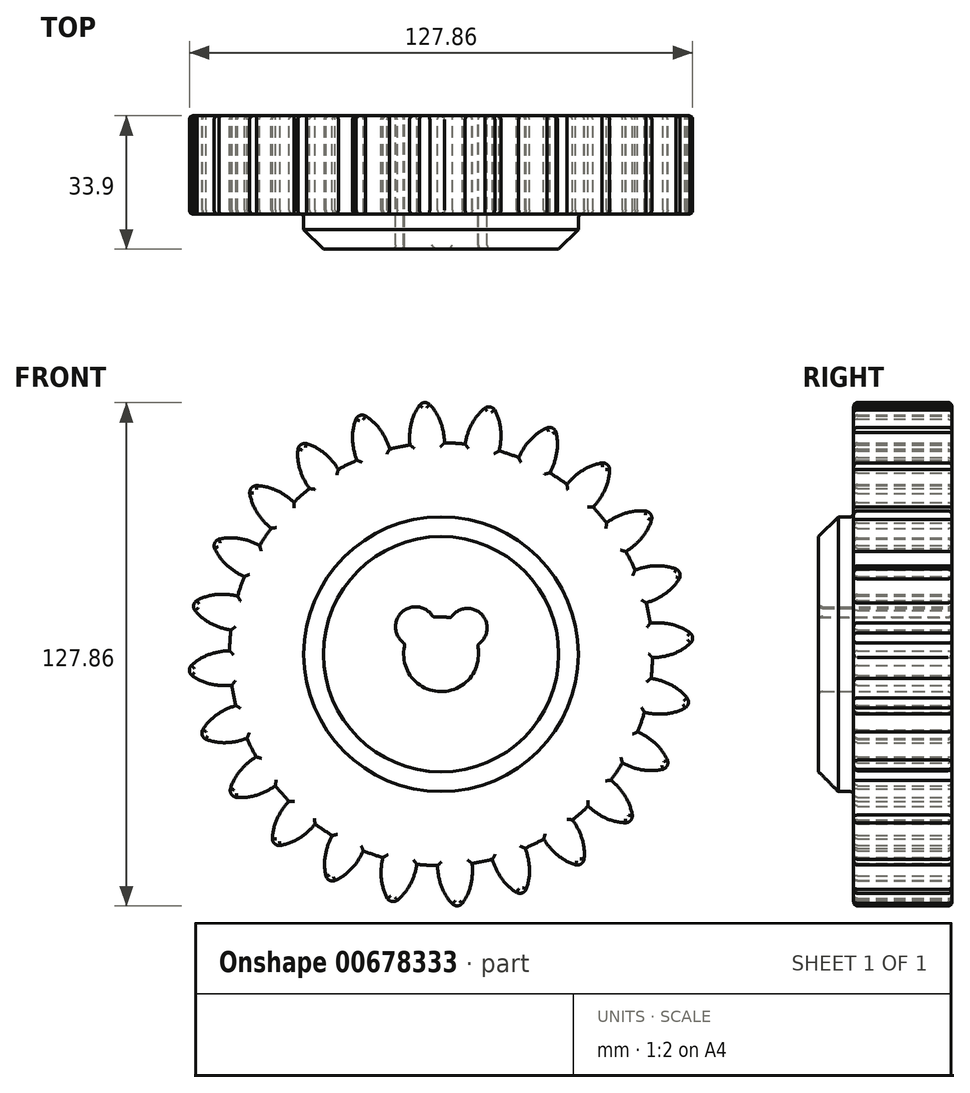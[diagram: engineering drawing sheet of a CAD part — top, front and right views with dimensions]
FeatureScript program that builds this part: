
annotation { "Feature Type Name" : "Feature", "Feature Type Description" : "" }
export const myFeature = defineFeature(function(context is Context, id is Id, definition is map)
    precondition{}
    {
        {
            var Q0;
            Q0=qCreatedBy(makeId("Front.planeOp"),FACE);
            var sketch = newSketch(context, id + "F0", { "sketchPlane" : qUnion([Q0])});
            skCircle(sketch, "E0", {"center": v(0, 0) * mm, "radius": 53.72 * mm});
            skCircle(sketch, "E1", {"center": v(0, 0) * mm, "radius": 58.67 * mm, "construction": true});
            skCircle(sketch, "E2", {"center": v(0, 0) * mm, "radius": 63.5 * mm, "construction": true});
            skLineSegment(sketch, "E3", {"start": v(0, 83.52) * mm, "end": v(0, 0) * mm, "construction": true});
            skLineSegment(sketch, "E4", {"start": v(0, 0) * mm, "end": v(-5.47, 83.52) * mm, "construction": true});
            skLineSegment(sketch, "E5", {"start": v(0, 58.67) * mm, "end": v(-56.46, 38.13) * mm, "construction": true});
            skLineSegment(sketch, "E6", {"start": v(0, 58.67) * mm, "end": v(-59.14, 58.67) * mm, "construction": true});
            skCircle(sketch, "E7", {"center": v(0, 0) * mm, "radius": 55.14 * mm, "construction": true});
            skCircle(sketch, "E8", {"center": v(0, 58.67) * mm, "radius": 14.6 * mm, "construction": true});
            skCircle(sketch, "E9", {"center": v(-13.72, 53.68) * mm, "radius": 14.6 * mm, "construction": true});
            skArc(sketch, "E10", {"start": v(0, 58.67) * mm, "mid": v(-1.18, 61.2) * mm, "end": v(-2.86, 63.44) * mm});
            skArc(sketch, "E11", {"start": v(0.88, 53.71) * mm, "mid": v(0.63, 56.23) * mm, "end": v(0, 58.67) * mm});
            skArc(sketch, "E12.MirrorCS", {"start": v(-7.66, 58.17) * mm, "mid": v(-6.82, 60.84) * mm, "end": v(-5.45, 63.27) * mm});
            skArc(sketch, "E13.MirrorCS", {"start": v(-7.88, 53.14) * mm, "mid": v(-7.97, 55.66) * mm, "end": v(-7.66, 58.17) * mm});
            skArc(sketch, "E14", {"start": v(-2.86, 63.44) * mm, "mid": v(-4.19, 63.92) * mm, "end": v(-5.45, 63.27) * mm});
            skCircle(sketch, "E15", {"center": v(0.01, 0) * mm, "radius": 34.89 * mm});
            skCircle(sketch, "E16", {"center": v(0.01, 0) * mm, "radius": 9.5 * mm});
            skCircle(sketch, "E17", {"center": v(-6.45, 6.97) * mm, "radius": 5.08 * mm});
            skCircle(sketch, "E18", {"center": v(6.77, 6.7) * mm, "radius": 4.94 * mm});
            skSolve(sketch);
        }
        {
            var Q0;
            Q0=makeQuery(id+"F0.imprint","IMPRINT",FACE,{"disambiguationData":[TD([[makeQuery(id+"F0.imprint","IMPRINT",EDGE,{"derivedFrom":sQuery(id+"F0.wireOp",EDGE,"E15")}),-1.0]])]});
            var Q1;
            Q1=makeQuery(id+"F0.imprint","IMPRINT",FACE,{"disambiguationData":[TD([[makeQuery(id+"F0.imprint","IMPRINT",EDGE,{"derivedFrom":sQuery(id+"F0.wireOp",EDGE,"E10")}),1.0]])]});
            extrude(context, id + "F1", {"entities" : qUnion([Q0, Q1]), "depth" : 25 * mm, "offsetDistance" : 25 * mm});
        }
        {
            var Q0;
            Q0=makeQuery(id+"F1.opExtrude","SWEPT_BODY",BODY,{"disambiguationData":[OSD([sQuery(id+"F0.wireOp",EDGE,"E0"),sQuery(id+"F0.wireOp",EDGE,"E10"),sQuery(id+"F0.wireOp",EDGE,"E11"),sQuery(id+"F0.wireOp",EDGE,"E12.MirrorCS"),sQuery(id+"F0.wireOp",EDGE,"E13.MirrorCS"),sQuery(id+"F0.wireOp",EDGE,"E14")])]});
            var Q1;
            Q1=makeQuery(id+"F1.opExtrude","SWEPT_FACE",FACE,{"disambiguationData":[OSD([sQuery(id+"F0.wireOp",EDGE,"E0")])]});
            circularPattern(context, id + "F2", {"entities" : qUnion([Q0]), "axis" : qUnion([Q1]), "angle" : 360 * degree, "instanceCount" : 24, "equalSpace" : true});
        }
        {
            var Q0;
            Q0=makeQuery(id+"F0.imprint","IMPRINT",FACE,{"disambiguationData":[TD([[makeQuery(id+"F0.imprint","IMPRINT",EDGE,{"derivedFrom":sQuery(id+"F0.wireOp",EDGE,"E15")}),1.0]])]});
            extrude(context, id + "F3", {"entities" : qUnion([Q0]), "operationType" : NewBodyOperationType.ADD, "depth" : 33.9 * mm, "offsetDistance" : 25 * mm});
        }
        {
            var Q0;
            Q0=makeQuery(id+"F3.opExtrude","CAP_EDGE",EDGE,{"disambiguationData":[OSD([sQuery(id+"F0.wireOp",EDGE,"E15")])],"isStart":true});
            var Q1;
            Q1=makeQuery(id+"F3.opExtrude","CAP_EDGE",EDGE,{"disambiguationData":[OSD([sQuery(id+"F0.wireOp",EDGE,"E15")])],"isStart":false});
            chamfer(context, id + "F4", {"entities" : qUnion([Q0, Q1]), "width" : 5 * mm, "tangentPropagation" : true});
        }
        {
            var Q0;
            {var subQ0=makeQuery(id+"F1.opExtrude","CAP_FACE",FACE,{"disambiguationData":[OSD([sQuery(id+"F0.wireOp",EDGE,"E0"),sQuery(id+"F0.wireOp",EDGE,"E10"),sQuery(id+"F0.wireOp",EDGE,"E11"),sQuery(id+"F0.wireOp",EDGE,"E12.MirrorCS"),sQuery(id+"F0.wireOp",EDGE,"E13.MirrorCS"),sQuery(id+"F0.wireOp",EDGE,"E14"),sQuery(id+"F0.wireOp",EDGE,"E15")])],"isStart":false});Q0=makeQuery(id+"F3.boolean.opBoolean","MERGE",FACE,{"derivedFrom":[subQ0,makeQuery(id+"F2.opPattern","COPY",FACE,{"derivedFrom":subQ0,"instanceName":"1"}),makeQuery(id+"F2.opPattern","COPY",FACE,{"derivedFrom":subQ0,"instanceName":"2"}),makeQuery(id+"F2.opPattern","COPY",FACE,{"derivedFrom":subQ0,"instanceName":"3"}),makeQuery(id+"F2.opPattern","COPY",FACE,{"derivedFrom":subQ0,"instanceName":"4"}),makeQuery(id+"F2.opPattern","COPY",FACE,{"derivedFrom":subQ0,"instanceName":"5"}),makeQuery(id+"F2.opPattern","COPY",FACE,{"derivedFrom":subQ0,"instanceName":"6"}),makeQuery(id+"F2.opPattern","COPY",FACE,{"derivedFrom":subQ0,"instanceName":"7"}),makeQuery(id+"F2.opPattern","COPY",FACE,{"derivedFrom":subQ0,"instanceName":"8"}),makeQuery(id+"F2.opPattern","COPY",FACE,{"derivedFrom":subQ0,"instanceName":"9"}),makeQuery(id+"F2.opPattern","COPY",FACE,{"derivedFrom":subQ0,"instanceName":"10"}),makeQuery(id+"F2.opPattern","COPY",FACE,{"derivedFrom":subQ0,"instanceName":"11"}),makeQuery(id+"F2.opPattern","COPY",FACE,{"derivedFrom":subQ0,"instanceName":"12"}),makeQuery(id+"F2.opPattern","COPY",FACE,{"derivedFrom":subQ0,"instanceName":"13"}),makeQuery(id+"F2.opPattern","COPY",FACE,{"derivedFrom":subQ0,"instanceName":"14"}),makeQuery(id+"F2.opPattern","COPY",FACE,{"derivedFrom":subQ0,"instanceName":"15"}),makeQuery(id+"F2.opPattern","COPY",FACE,{"derivedFrom":subQ0,"instanceName":"16"}),makeQuery(id+"F2.opPattern","COPY",FACE,{"derivedFrom":subQ0,"instanceName":"17"}),makeQuery(id+"F2.opPattern","COPY",FACE,{"derivedFrom":subQ0,"instanceName":"18"}),makeQuery(id+"F2.opPattern","COPY",FACE,{"derivedFrom":subQ0,"instanceName":"19"}),makeQuery(id+"F2.opPattern","COPY",FACE,{"derivedFrom":subQ0,"instanceName":"20"}),makeQuery(id+"F2.opPattern","COPY",FACE,{"derivedFrom":subQ0,"instanceName":"21"}),makeQuery(id+"F2.opPattern","COPY",FACE,{"derivedFrom":subQ0,"instanceName":"22"}),makeQuery(id+"F2.opPattern","COPY",FACE,{"derivedFrom":subQ0,"instanceName":"23"})]});}
            var Q1;
            {var subQ0=sQuery(id+"F0.wireOp",EDGE,"E15");var subQ1=makeQuery(id+"F1.opExtrude","CAP_FACE",FACE,{"disambiguationData":[OSD([sQuery(id+"F0.wireOp",EDGE,"E0"),sQuery(id+"F0.wireOp",EDGE,"E10"),sQuery(id+"F0.wireOp",EDGE,"E11"),sQuery(id+"F0.wireOp",EDGE,"E12.MirrorCS"),sQuery(id+"F0.wireOp",EDGE,"E13.MirrorCS"),sQuery(id+"F0.wireOp",EDGE,"E14"),subQ0])],"isStart":true});Q1=makeQuery(id+"F3.boolean.opBoolean","MERGE",FACE,{"derivedFrom":[subQ1,makeQuery(id+"F2.opPattern","COPY",FACE,{"derivedFrom":subQ1,"instanceName":"1"}),makeQuery(id+"F2.opPattern","COPY",FACE,{"derivedFrom":subQ1,"instanceName":"2"}),makeQuery(id+"F2.opPattern","COPY",FACE,{"derivedFrom":subQ1,"instanceName":"3"}),makeQuery(id+"F2.opPattern","COPY",FACE,{"derivedFrom":subQ1,"instanceName":"4"}),makeQuery(id+"F2.opPattern","COPY",FACE,{"derivedFrom":subQ1,"instanceName":"5"}),makeQuery(id+"F2.opPattern","COPY",FACE,{"derivedFrom":subQ1,"instanceName":"6"}),makeQuery(id+"F2.opPattern","COPY",FACE,{"derivedFrom":subQ1,"instanceName":"7"}),makeQuery(id+"F2.opPattern","COPY",FACE,{"derivedFrom":subQ1,"instanceName":"8"}),makeQuery(id+"F2.opPattern","COPY",FACE,{"derivedFrom":subQ1,"instanceName":"9"}),makeQuery(id+"F2.opPattern","COPY",FACE,{"derivedFrom":subQ1,"instanceName":"10"}),makeQuery(id+"F2.opPattern","COPY",FACE,{"derivedFrom":subQ1,"instanceName":"11"}),makeQuery(id+"F2.opPattern","COPY",FACE,{"derivedFrom":subQ1,"instanceName":"12"}),makeQuery(id+"F2.opPattern","COPY",FACE,{"derivedFrom":subQ1,"instanceName":"13"}),makeQuery(id+"F2.opPattern","COPY",FACE,{"derivedFrom":subQ1,"instanceName":"14"}),makeQuery(id+"F2.opPattern","COPY",FACE,{"derivedFrom":subQ1,"instanceName":"15"}),makeQuery(id+"F2.opPattern","COPY",FACE,{"derivedFrom":subQ1,"instanceName":"16"}),makeQuery(id+"F2.opPattern","COPY",FACE,{"derivedFrom":subQ1,"instanceName":"17"}),makeQuery(id+"F2.opPattern","COPY",FACE,{"derivedFrom":subQ1,"instanceName":"18"}),makeQuery(id+"F2.opPattern","COPY",FACE,{"derivedFrom":subQ1,"instanceName":"19"}),makeQuery(id+"F2.opPattern","COPY",FACE,{"derivedFrom":subQ1,"instanceName":"20"}),makeQuery(id+"F2.opPattern","COPY",FACE,{"derivedFrom":subQ1,"instanceName":"21"}),makeQuery(id+"F2.opPattern","COPY",FACE,{"derivedFrom":subQ1,"instanceName":"22"}),makeQuery(id+"F2.opPattern","COPY",FACE,{"derivedFrom":subQ1,"instanceName":"23"}),makeQuery(id+"F3.opExtrude","CAP_FACE",FACE,{"disambiguationData":[OSD([subQ0,sQuery(id+"F0.wireOp",EDGE,"E16"),sQuery(id+"F0.wireOp",EDGE,"E17"),sQuery(id+"F0.wireOp",EDGE,"E18")])],"isStart":true})]});}
            var Q2;
            Q2=makeQuery(id+"F3.opExtrude","SWEPT_FACE",FACE,{"disambiguationData":[OSD([sQuery(id+"F0.wireOp",EDGE,"E17")])]});
            var Q3;
            {var subQ0=sQuery(id+"F0.wireOp",EDGE,"E16");Q3=makeQuery(id+"F3.opExtrude","SWEPT_FACE",FACE,{"disambiguationData":[OSD([subQ0]),TDD([makeQuery(id+"F0.imprint","IMPRINT",EDGE,{"disambiguationData":[TD([[makeQuery(id+"F0.imprint","INTERSECT",VERTEX,{"disambiguationData":[OD(1.0)],"derivedFrom":[subQ0,sQuery(id+"F0.wireOp",EDGE,"E18")]}),1.0]])],"derivedFrom":subQ0})])]});}
            var Q4;
            Q4=makeQuery(id+"F3.opExtrude","SWEPT_FACE",FACE,{"disambiguationData":[OSD([sQuery(id+"F0.wireOp",EDGE,"E18")])]});
            var Q5;
            {var subQ0=sQuery(id+"F0.wireOp",EDGE,"E18");var subQ1=sQuery(id+"F0.wireOp",EDGE,"E16");Q5=makeQuery(id+"F3.opExtrude","SWEPT_EDGE",EDGE,{"disambiguationData":[OSD([subQ1,subQ0]),TDD([makeQuery(id+"F0.imprint","INTERSECT",VERTEX,{"disambiguationData":[OD(0.0)],"derivedFrom":[subQ1,subQ0]})])]});}
            fillet(context, id + "F5", {"entities" : qUnion([Q0, Q1, Q2, Q3, Q4, Q5]), "radius" : 1 * mm, "tangentPropagation" : true, "allowEdgeOverflow" : false});
        }
    });
